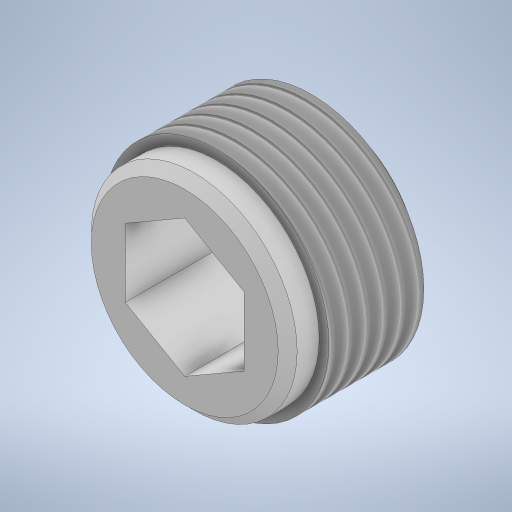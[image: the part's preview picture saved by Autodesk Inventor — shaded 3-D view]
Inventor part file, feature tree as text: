
AUTODESK INVENTOR PART (.ipt)
format: ipt  version: 2024 (Build 280153000, 153)  size: 334,848 bytes
history: native  units: in
note: dims shown in document units (in); Inventor stores cm internally (conversion verified against a paired STEP export)
features: extrude x5, sketch x5, projected_geometry x2, chamfer x1, thread x1, mirror x1
ambient origin geometry x8: Origin, YZ Plane, XZ Plane, XY Plane, X Axis, Y Axis, Z Axis, Center Point
bodies: Solid1 (feature_tree), Solid2 (feature_tree)
feature tree (15):
  extrude  "Extrusion1"  Depth=0.2in TaperAngle=0.0deg
  extrude  "Extrusion2"  Depth=0.025in
  extrude  "Extrusion3"  Depth=0.05in TaperAngle=0.0deg
  chamfer  "Chamfer1"  Distance=0.015in Angle=45.0deg
  extrude  "Extrusion4"  Depth=0.15in TaperAngle=0.0deg
  thread  "Thread1"  [1 undecoded]
  mirror  "Mirror1"
  extrude  "Extrusion5"  [1 undecoded]
  sketch  "Sketch1"  dims[d0=0.355in d1=0.2in d2=0.0in]
  sketch  "Sketch2"  dims[d3=0.3in d4=0.025in d5=-0.1031in]
  sketch  "Sketch3"  dims[d6=0.325in d7=0.05in d8=0.0in d9=0.015in d10=0.125in d11=45.0deg]
  projected_geometry  "Projected Loop1"
  sketch  "Sketch4"  dims[d12=0.1875in d13=100.0in d14=0.0in d15=0.15in d16=0.0in]
  sketch  "Sketch6"  dims[d17=0.25in d18=0.0in]
  projected_geometry  "Project Cut Edges1"
note: 2 required parameter values undecoded (feature->parameter linkage not recoverable at this tier; creation-order binding heuristic only, values carry confidence <= 0.55)
